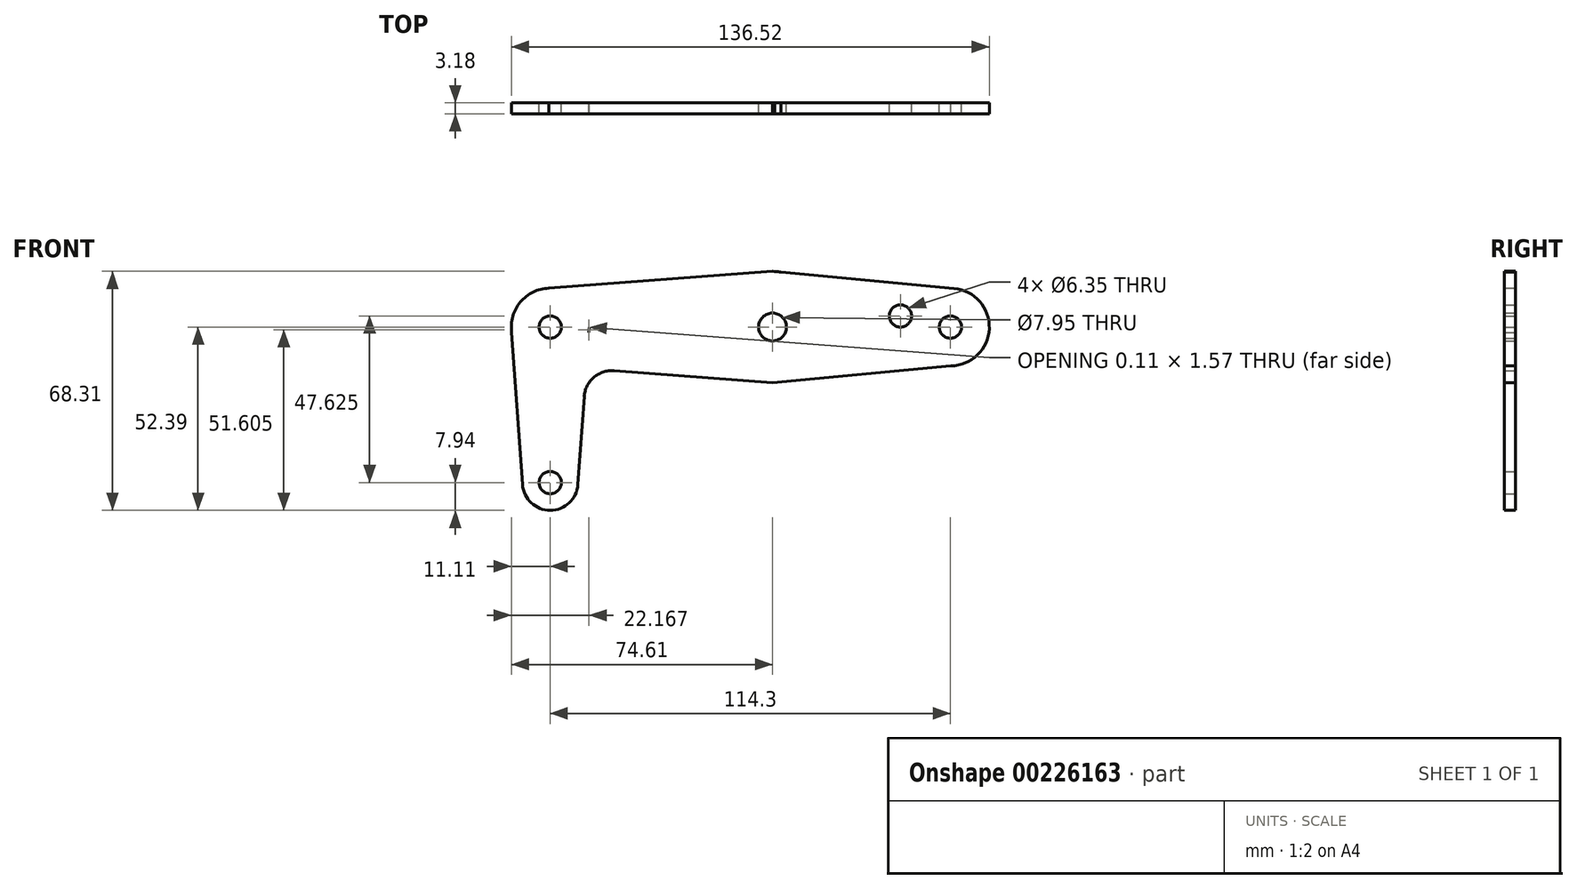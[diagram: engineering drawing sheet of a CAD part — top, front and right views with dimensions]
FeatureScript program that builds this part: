
annotation { "Feature Type Name" : "Feature", "Feature Type Description" : "" }
export const myFeature = defineFeature(function(context is Context, id is Id, definition is map)
    precondition{}
    {
        {
            var Q0;
            Q0=qCreatedBy(makeId("Front.planeOp"),FACE);
            var sketch = newSketch(context, id + "F0", { "sketchPlane" : qUnion([Q0])});
            skCircle(sketch, "E0", {"center": v(0, 0) * mm, "radius": 3.98 * mm});
            skCircle(sketch, "E1", {"center": v(0, 0) * mm, "radius": 15.88 * mm});
            skLineSegment(sketch, "E2", {"start": v(0, 0) * mm, "end": v(50.8, 0) * mm});
            skLineSegment(sketch, "E3", {"start": v(0, 0) * mm, "end": v(-63.5, 0) * mm});
            skCircle(sketch, "E4", {"center": v(36.53, 3.18) * mm, "radius": 3.18 * mm});
            skCircle(sketch, "E5", {"center": v(50.8, 0) * mm, "radius": 11.11 * mm});
            skCircle(sketch, "E6", {"center": v(50.8, 0) * mm, "radius": 3.18 * mm});
            skCircle(sketch, "E7", {"center": v(-63.5, 0) * mm, "radius": 11.11 * mm});
            skLineSegment(sketch, "E8", {"start": v(-63.5, 0) * mm, "end": v(-63.5, -3.18) * mm});
            skCircle(sketch, "E9", {"center": v(-63.5, -44.45) * mm, "radius": 7.94 * mm});
            skCircle(sketch, "E10", {"center": v(-63.5, -44.45) * mm, "radius": 3.18 * mm});
            skCircle(sketch, "E11", {"center": v(-63.5, 0) * mm, "radius": 3.18 * mm});
            skCircle(sketch, "E12", {"center": v(0, 0) * mm, "radius": 3.18 * mm});
            skLineSegment(sketch, "E13", {"start": v(-63.87, 11.1) * mm, "end": v(0, 15.92) * mm});
            skLineSegment(sketch, "E14", {"start": v(0, 15.92) * mm, "end": v(51.84, 11.06) * mm});
            skLineSegment(sketch, "E15", {"start": v(-74.61, 0) * mm, "end": v(-71.42, -45.01) * mm});
            skLineSegment(sketch, "E16", {"start": v(50.93, -11.11) * mm, "end": v(0, -15.95) * mm});
            skLineSegment(sketch, "E17", {"start": v(0, -15.95) * mm, "end": v(-45.26, -12.5) * mm});
            skLineSegment(sketch, "E18", {"start": v(-52.39, 0) * mm, "end": v(-52.5, -1.57) * mm});
            skLineSegment(sketch, "E19.trimOffspring", {"start": v(-53.8, -19.87) * mm, "end": v(-55.58, -45.01) * mm});
            skPoint(sketch, "E20.visualSharp", {"position": v(-53.23, -11.9) * mm});
            skArc(sketch, "E20.filletArc", {"start": v(-45.26, -12.5) * mm, "mid": v(-51.06, -14.4) * mm, "end": v(-53.8, -19.87) * mm});
            skLineSegment(sketch, "E21.trimOffspring", {"start": v(-63.5, -11.11) * mm, "end": v(-63.5, -44.45) * mm});
            skLineSegment(sketch, "E22", {"start": v(-63.5, -3.18) * mm, "end": v(-63.5, -11.11) * mm});
            skSolve(sketch);
        }
        {
            var Q0;
            Q0 = qSketchRegion(id + "F0", true);
            var Q1;
            {var subQ7=sQuery(id+"F0.wireOp",EDGE,"E18");Q1=makeQuery(id+"F0.imprint","IMPRINT",FACE,{"disambiguationData":[TD([[makeQuery(id+"F0.imprint","IMPRINT",EDGE,{"derivedFrom":subQ7}),-1.0]])]});}
            extrude(context, id + "F1", {"entities" : qUnion([Q0, Q1]), "depth" : 3.17 * mm});
        }
    });
